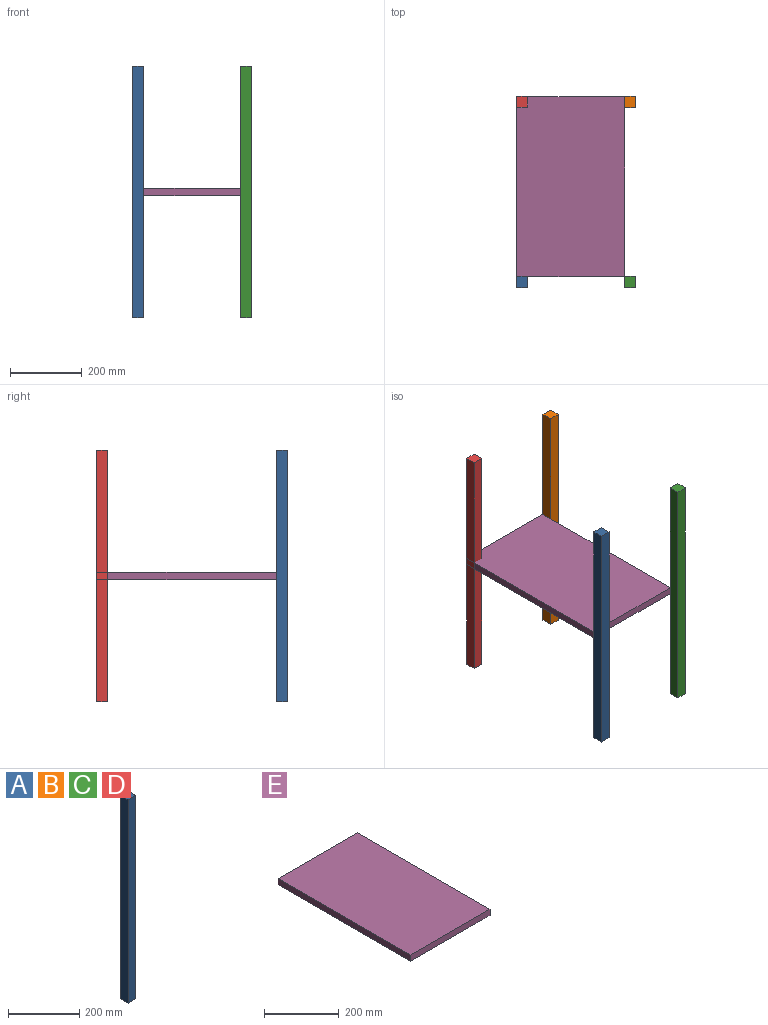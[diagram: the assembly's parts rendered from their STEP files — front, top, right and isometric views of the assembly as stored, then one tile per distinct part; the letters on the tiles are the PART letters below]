
ASSEMBLY  parts=5 mates=2
PART A: 6 faces, bbox 30x30x700 mm
  f0: plane 700x30mm, normal (0,-1,0), area 21000mm2, adj f1,f3,f4,f5
  f1: plane 700x30mm, normal (1,0,0), area 21000mm2, adj f0,f2,f4,f5
  f2: plane 700x30mm, normal (0,1,0), area 21000mm2, adj f1,f3,f4,f5
  f3: plane 700x30mm, normal (-1,0,0), area 21000mm2, adj f0,f2,f4,f5
  f4: plane 30x30mm, normal (0,0,1), area 900mm2, adj f0,f1,f2,f3
  f5: plane 30x30mm, normal (0,0,-1), area 900mm2, adj f0,f1,f2,f3
PART B: same geometry as A
PART C: same geometry as A
PART D: same geometry as A
PART E: 6 faces, bbox 300x500x20 mm
  f0: plane 300x20mm, normal (0,-1,0), area 6000mm2, adj f1,f3,f4,f5
  f1: plane 500x20mm, normal (1,0,0), area 10000mm2, adj f0,f2,f4,f5
  f2: plane 300x20mm, normal (0,1,0), area 6000mm2, adj f1,f3,f4,f5
  f3: plane 500x20mm, normal (-1,0,0), area 10000mm2, adj f0,f2,f4,f5
  f4: plane 500x300mm, normal (0,0,1), area 150000mm2, adj f0,f1,f2,f3
  f5: plane 500x300mm, normal (0,0,-1), area 150000mm2, adj f0,f1,f2,f3
PLACE A t=(-349.59,20.27,73.36)mm
PLACE B t=(-49.59,520.27,73.36)mm
PLACE C t=(-49.59,20.27,73.36)mm fixed
PLACE D t=(-349.59,520.27,73.36)mm
PLACE E t=(-214.59,285.27,413.36)mm
MATE planar C.f3 <-> E.f1  axis (-1,0,0) through (-64.59,20.27,423.36)mm
MATE planar E.f0 <-> C.f2  axis (0,-1,0) through (-214.59,35.27,423.36)mm
